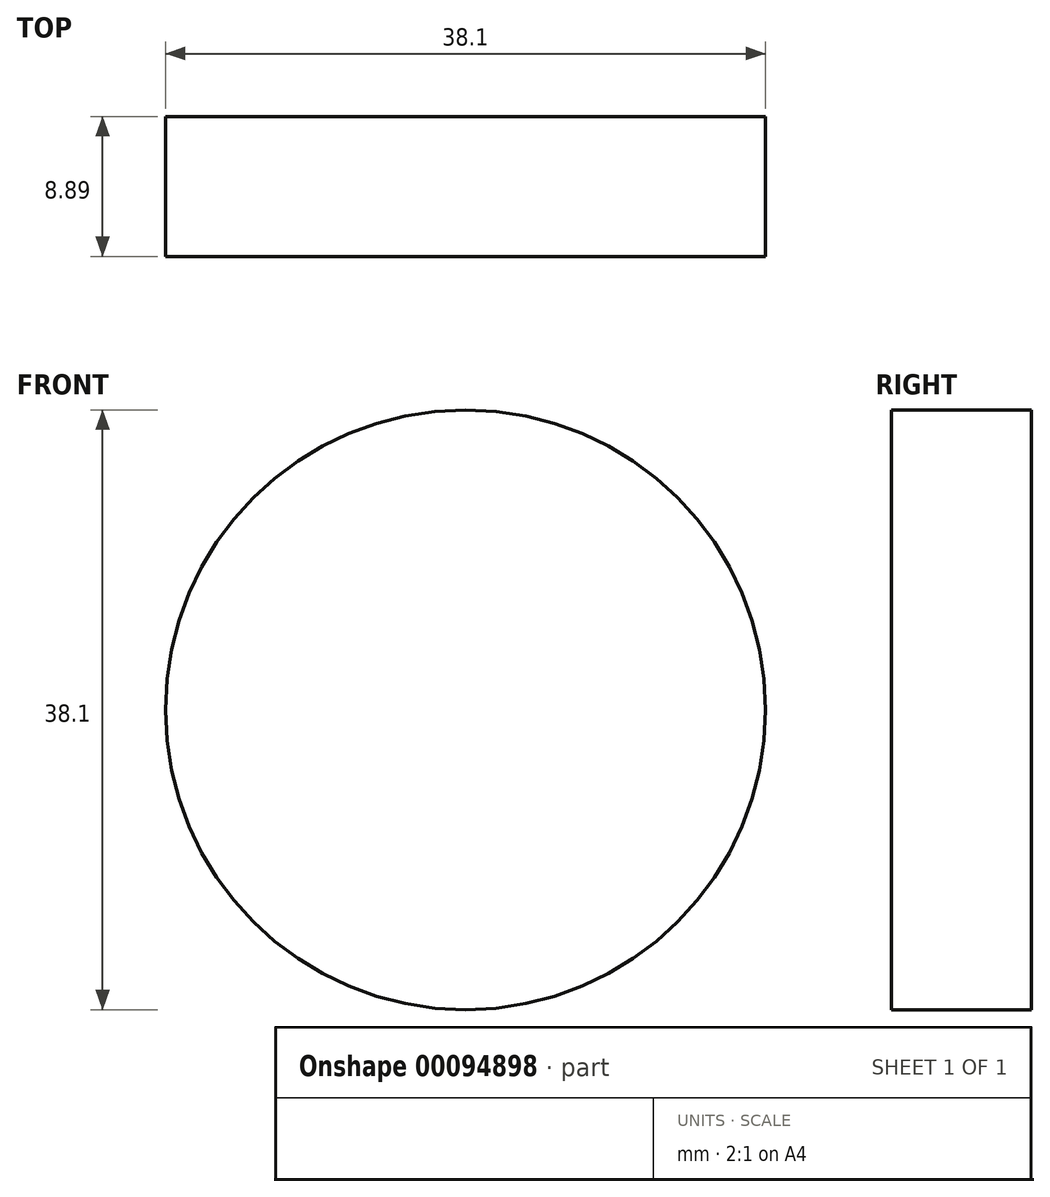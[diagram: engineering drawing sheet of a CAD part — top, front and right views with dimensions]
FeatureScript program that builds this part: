
annotation { "Feature Type Name" : "Feature", "Feature Type Description" : "" }
export const myFeature = defineFeature(function(context is Context, id is Id, definition is map)
    precondition{}
    {
        {
            var Q0;
            Q0=qCreatedBy(makeId("Front.planeOp"),FACE);
            var sketch = newSketch(context, id + "F0", { "sketchPlane" : qUnion([Q0])});
            skCircle(sketch, "E0", {"center": v(19.05, 19.05) * mm, "radius": 19.05 * mm});
            skSolve(sketch);
        }
        {
            var Q0;
            Q0 = qSketchRegion(id + "F0", true);
            extrude(context, id + "F1", {"entities" : qUnion([Q0]), "depth" : 8.9 * mm});
        }
    });
